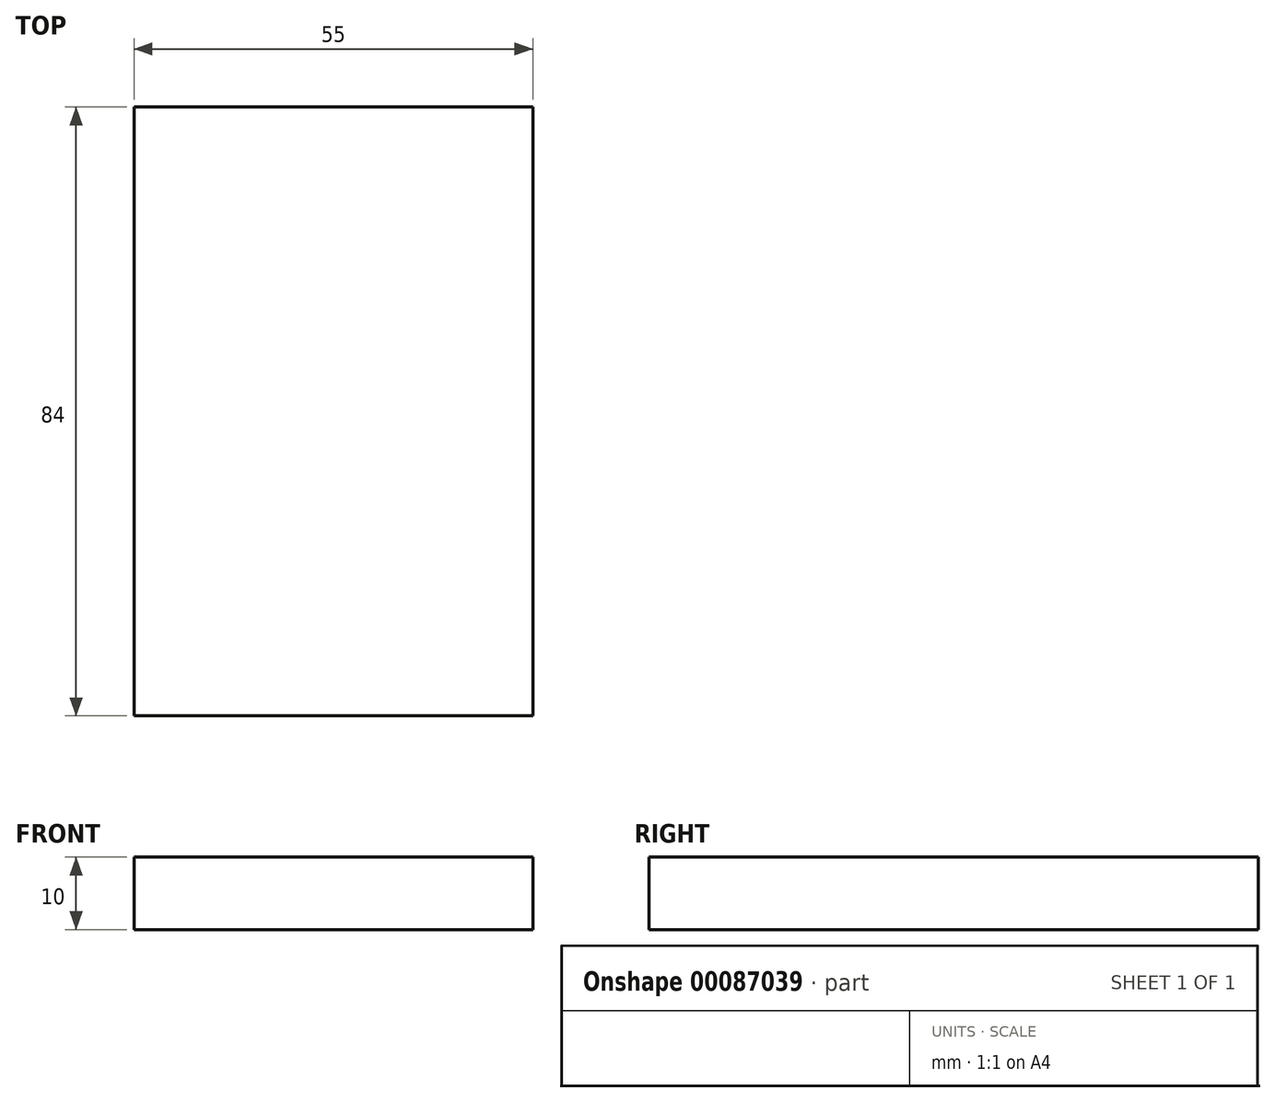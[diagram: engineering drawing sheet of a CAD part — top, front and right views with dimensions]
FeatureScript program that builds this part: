
annotation { "Feature Type Name" : "Feature", "Feature Type Description" : "" }
export const myFeature = defineFeature(function(context is Context, id is Id, definition is map)
    precondition{}
    {
        {
            var Q0;
            Q0=qCreatedBy(makeId("Top.planeOp"),FACE);
            var sketch = newSketch(context, id + "F0", { "sketchPlane" : qUnion([Q0])});
            skLineSegment(sketch, "E0.bottom", {"start": v(27.5, 42) * mm, "end": v(-27.5, 42) * mm});
            skLineSegment(sketch, "E0.top", {"start": v(27.5, -42) * mm, "end": v(-27.5, -42) * mm});
            skLineSegment(sketch, "E0.left", {"start": v(27.5, 42) * mm, "end": v(27.5, -42) * mm});
            skLineSegment(sketch, "E0.right", {"start": v(-27.5, 42) * mm, "end": v(-27.5, -42) * mm});
            skPoint(sketch, "E0.middle", {"position": v(0, 0) * mm});
            skSolve(sketch);
        }
        {
            var Q0;
            Q0=makeQuery(id+"F0.imprint","IMPRINT",FACE,{"disambiguationData":[TD([[makeQuery(id+"F0.imprint","IMPRINT",EDGE,{"derivedFrom":sQuery(id+"F0.wireOp",EDGE,"E0.bottom")}),1.0]])]});
            extrude(context, id + "F1", {"entities" : qUnion([Q0]), "depth" : 10 * mm});
        }
    });
